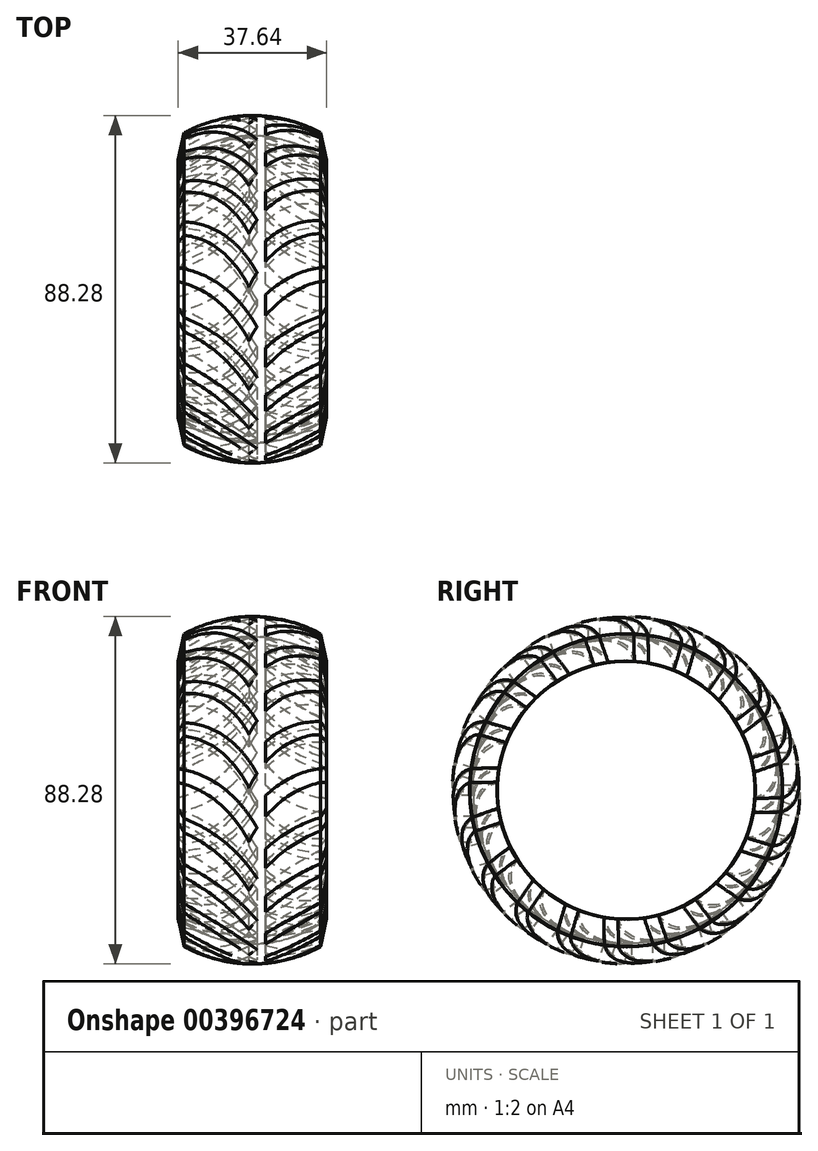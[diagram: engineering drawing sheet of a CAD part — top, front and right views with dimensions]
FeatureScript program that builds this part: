
annotation { "Feature Type Name" : "Feature", "Feature Type Description" : "" }
export const myFeature = defineFeature(function(context is Context, id is Id, definition is map)
    precondition{}
    {
        {
            var Q0;
            Q0=qCreatedBy(makeId("Front.planeOp"),FACE);
            var sketch = newSketch(context, id + "F0", { "sketchPlane" : qUnion([Q0])});
            skArc(sketch, "E0", {"start": v(0.18, 39.06) * mm, "mid": v(-9.78, 37.45) * mm, "end": v(-18.73, 32.78) * mm});
            skPoint(sketch, "E1.endSnap0", {"position": v(0.18, 39.06) * mm});
            skArc(sketch, "E2.0", {"start": v(0.1, 44.14) * mm, "mid": v(-8.84, 43.01) * mm, "end": v(-17.23, 39.74) * mm});
            skPoint(sketch, "E3.orphan", {"position": v(-19.3, 19.38) * mm});
            skPoint(sketch, "E4.orphan", {"position": v(-37.7, 19.38) * mm});
            skPoint(sketch, "E5.orphan", {"position": v(19.3, 19.38) * mm});
            skLineSegment(sketch, "E6", {"start": v(-17.23, 39.74) * mm, "end": v(-18.73, 32.78) * mm});
            skArc(sketch, "E7.MirrorCS", {"start": v(0.1, 44.14) * mm, "mid": v(9.03, 43.01) * mm, "end": v(17.42, 39.74) * mm});
            skLineSegment(sketch, "E8.MirrorCS", {"start": v(17.42, 39.74) * mm, "end": v(18.91, 32.78) * mm});
            skArc(sketch, "E9.MirrorCS", {"start": v(0, 39.06) * mm, "mid": v(9.96, 37.45) * mm, "end": v(18.91, 32.78) * mm});
            skLineSegment(sketch, "E10", {"start": v(-31.31, 0) * mm, "end": v(36.78, 0) * mm});
            skSolve(sketch);
        }
        {
            var Q0;
            Q0=makeQuery(id+"F0.imprint","IMPRINT",FACE,{"disambiguationData":[TD([[makeQuery(id+"F0.imprint","IMPRINT",EDGE,{"derivedFrom":sQuery(id+"F0.wireOp",EDGE,"E2.0")}),1.0]])]});
            var Q1;
            Q1=sQuery(id+"F0.wireOp",EDGE,"E10");
            revolve(context, id + "F1", {"entities" : qUnion([Q0]), "axis" : qUnion([Q1]), "revolveType" : RevolveType.FULL});
        }
        {
            var Q0;
            Q0=qCreatedBy(makeId("Front.planeOp"),FACE);
            cPlane(context, id + "F2", {"entities" : qUnion([Q0]), "cplaneType" : CPlaneType.OFFSET, "offset" : 76.2 * mm, "width" : 152.4 * mm, "height" : 152.4 * mm});
        }
        {
            var Q0;
            Q0=qCreatedBy(id+"F2.planeOp",FACE);
            var sketch = newSketch(context, id + "F3", { "sketchPlane" : qUnion([Q0])});
            skFitSpline(sketch, "E11", {"points": [v(-23.82, 5.75) * mm, v(5.54, -19.57) * mm], "startDerivative": vector(32.8, 1.73) * mm, "endDerivative": vector(17.98, -57.85) * mm});
            skFitSpline(sketch, "E12.0", {"points": [v(-23.62, 1.95) * mm, v(-21.3, 2.07) * mm, v(-17.73, 1.68) * mm, v(-13.03, -0.2) * mm, v(-9.58, -2.35) * mm, v(-6.27, -5.35) * mm, v(-2.14, -10.63) * mm, v(0.5, -16.18) * mm, v(1.9, -20.7) * mm]});
            skLineSegment(sketch, "E13", {"start": v(-5.09, -6.93) * mm, "end": v(-5.09, -1.33) * mm});
            skLineSegment(sketch, "E14", {"start": v(-23.82, 5.75) * mm, "end": v(-23.62, 1.95) * mm});
            skLineSegment(sketch, "E15.MirrorCS", {"start": v(3.5, -6.93) * mm, "end": v(3.5, -1.33) * mm});
            skFitSpline(sketch, "E16.MirrorCS", {"points": [v(22.23, 5.75) * mm, v(-7.13, -19.57) * mm], "startDerivative": vector(-32.8, 1.73) * mm, "endDerivative": vector(-17.98, -57.85) * mm});
            skLineSegment(sketch, "E17.MirrorCS", {"start": v(22.23, 5.75) * mm, "end": v(22.03, 1.95) * mm});
            skFitSpline(sketch, "E18.0", {"points": [v(22.03, 1.95) * mm, v(19.72, 2.07) * mm, v(16.14, 1.68) * mm, v(11.43, -0.2) * mm, v(7.99, -2.35) * mm, v(4.68, -5.35) * mm, v(0.55, -10.63) * mm, v(-2.08, -16.18) * mm, v(-3.49, -20.7) * mm]});
            skArc(sketch, "E19", {"start": v(6.1, -4.11) * mm, "mid": v(4.75, -5.47) * mm, "end": v(3.5, -6.93) * mm});
            skSolve(sketch);
        }
        {
            var Q0;
            Q0=makeQuery(id+"F3.imprint","IMPRINT",FACE,{"disambiguationData":[TD([[makeQuery(id+"F3.imprint","IMPRINT",EDGE,{"derivedFrom":sQuery(id+"F3.wireOp",EDGE,"E11")}),-1.0]])]});
            var Q1;
            Q1=makeQuery(id+"F3.imprint","IMPRINT",FACE,{"disambiguationData":[TD([[makeQuery(id+"F3.imprint","IMPRINT",EDGE,{"derivedFrom":sQuery(id+"F3.wireOp",EDGE,"E15.MirrorCS")}),-1.0]])]});
            extrude(context, id + "F4", {"entities" : qUnion([Q0, Q1]), "operationType" : NewBodyOperationType.REMOVE, "oppositeDirection" : true, "depth" : 70.61 * mm});
        }
        {
            var Q0;
            Q0=makeQuery(id+"F1.opRevolve","SWEPT_BODY",BODY,{"disambiguationData":[OSD([sQuery(id+"F0.wireOp",EDGE,"E0"),sQuery(id+"F0.wireOp",EDGE,"E2.0"),sQuery(id+"F0.wireOp",EDGE,"E6"),sQuery(id+"F0.wireOp",EDGE,"E7.MirrorCS"),sQuery(id+"F0.wireOp",EDGE,"E8.MirrorCS"),sQuery(id+"F0.wireOp",EDGE,"E9.MirrorCS")])]});
            var Q1;
            Q1=makeQuery(id+"F1.opRevolve","SWEPT_FACE",FACE,{"disambiguationData":[OSD([sQuery(id+"F0.wireOp",EDGE,"E6")])]});
            circularPattern(context, id + "F5", {"entities" : qUnion([Q0]), "axis" : qUnion([Q1]), "angle" : 360 * degree, "instanceCount" : 20, "equalSpace" : true});
        }
    });
